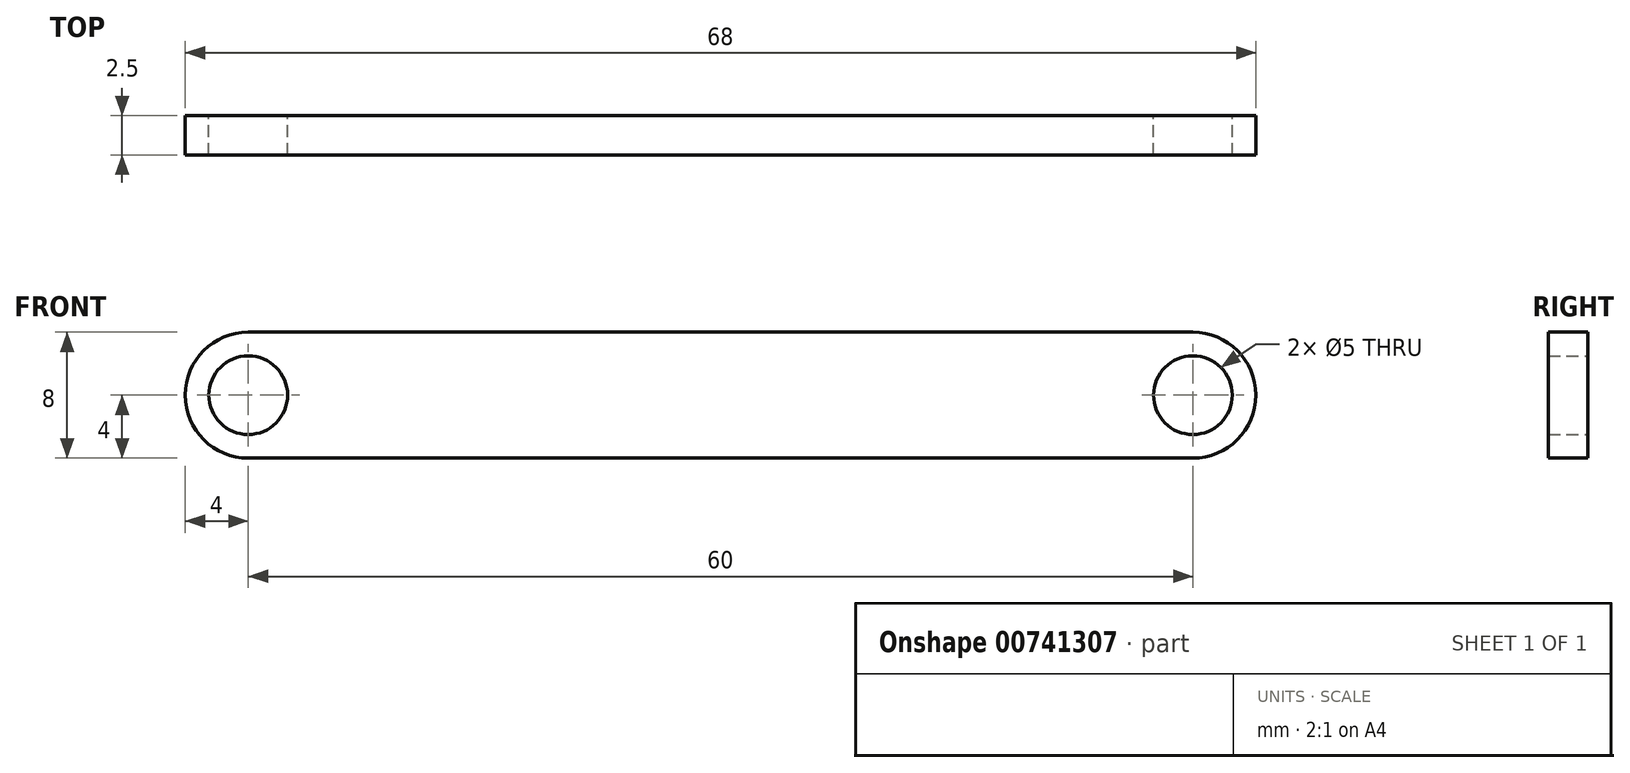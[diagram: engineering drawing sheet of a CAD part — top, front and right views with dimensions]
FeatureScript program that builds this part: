
annotation { "Feature Type Name" : "Feature", "Feature Type Description" : "" }
export const myFeature = defineFeature(function(context is Context, id is Id, definition is map)
    precondition{}
    {
        {
            var Q0;
            Q0=qCreatedBy(makeId("Front.planeOp"),FACE);
            var sketch = newSketch(context, id + "F0", { "sketchPlane" : qUnion([Q0])});
            skCircle(sketch, "E0", {"center": v(0, 0) * mm, "radius": 2.5 * mm});
            skArc(sketch, "E1", {"start": v(0, 4) * mm, "mid": v(-4, 0) * mm, "end": v(0, -4) * mm});
            skLineSegment(sketch, "E2", {"start": v(0, 0) * mm, "end": v(2.5, 0) * mm});
            skCircle(sketch, "E3", {"center": v(60, 0) * mm, "radius": 2.5 * mm});
            skArc(sketch, "E4", {"start": v(60, -4) * mm, "mid": v(64, 0) * mm, "end": v(60, 4) * mm});
            skLineSegment(sketch, "E5", {"start": v(0, -4) * mm, "end": v(60, -4) * mm});
            skLineSegment(sketch, "E6", {"start": v(0, 4) * mm, "end": v(60, 4) * mm});
            skLineSegment(sketch, "E7.trimOffspring", {"start": v(57.5, 0) * mm, "end": v(60, 0) * mm});
            skSolve(sketch);
        }
        {
            var Q0;
            Q0=makeQuery(id+"F0.imprint","IMPRINT",FACE,{"disambiguationData":[TD([[makeQuery(id+"F0.imprint","IMPRINT",EDGE,{"derivedFrom":sQuery(id+"F0.wireOp",EDGE,"E0")}),-1.0]])]});
            extrude(context, id + "F1", {"entities" : qUnion([Q0]), "depth" : 2.5 * mm, "offsetDistance" : 25.4 * mm});
        }
    });
